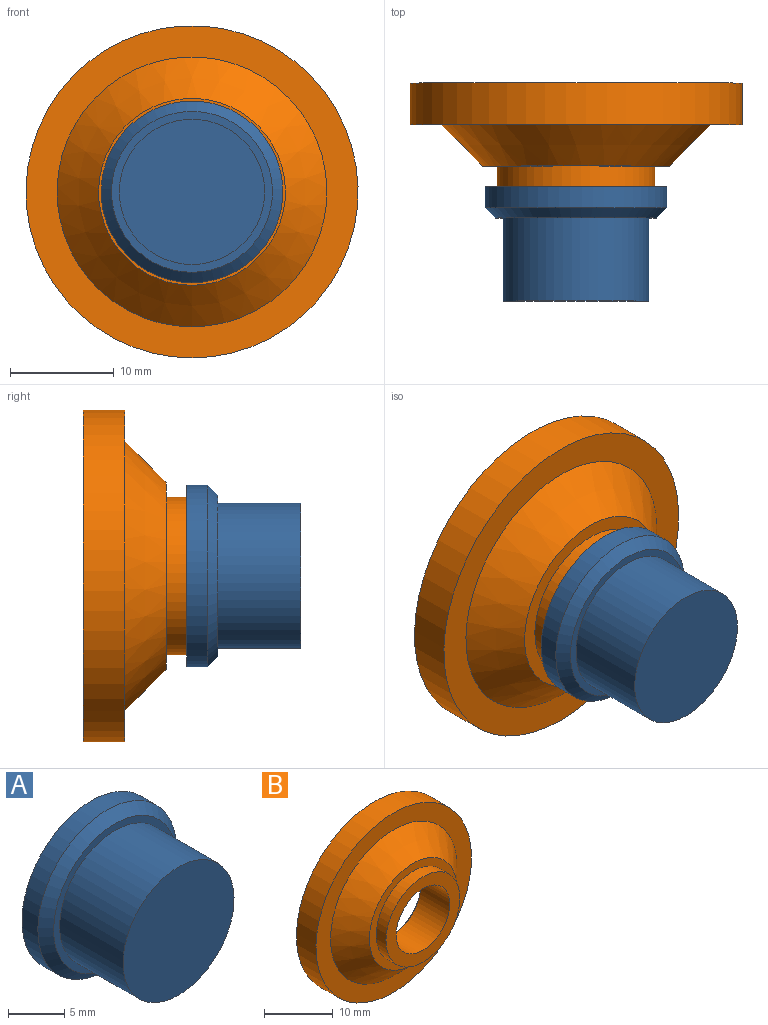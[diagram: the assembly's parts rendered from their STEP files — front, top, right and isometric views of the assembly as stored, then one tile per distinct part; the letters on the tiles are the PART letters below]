
ASSEMBLY  parts=2 mates=1
PART A: 6 faces, bbox 17.5x11x17.5 mm
  f0: cylinder r=8.75mm len=17.5mm, axis (0,1,0), area 110mm2, adj f2,f5
  f1: plane 15.5x15.5mm, normal (0,-1,0), area 34.8mm2, adj f3,f5
  f2: plane 17.5x17.5mm, normal (0,1,0), area 240.5mm2, adj f0
  f3: cylinder r=7mm len=14mm, axis (0,1,0), area 351.9mm2, adj f1,f4
  f4: plane 14x14mm, normal (0,-1,0), area 153.9mm2, adj f3
  f5: cone r=7.75mm half-angle=45deg, axis (0,1,0), area 73.3mm2, adj f0,f1
PART B: 10 faces, bbox 32x10x32 mm
  f0: cylinder r=5.5mm len=11mm, axis (0,1,0), area 207.3mm2, adj f2,f9
  f1: cylinder r=7.6mm len=15.2mm, axis (0,1,0), area 95.5mm2, adj f2,f4
  f2: plane 15.2x15.2mm, normal (0,-1,0), area 86.4mm2, adj f0,f1
  f3: plane 32x32mm, normal (0,1,0), area 424.1mm2, adj f6,f8
  f4: plane 18x18mm, normal (0,-1,0), area 73mm2, adj f1,f5
  f5: cone r=9mm half-angle=45deg, axis (0,1,0), area 391mm2, adj f4,f7
  f6: cylinder r=16mm len=32mm, axis (0,1,0), area 402.1mm2, adj f3,f7
  f7: plane 32x32mm, normal (0,-1,0), area 273.3mm2, adj f5,f6
  f8: cylinder r=11mm len=22mm, axis (0,1,0), area 276.5mm2, adj f3,f9
  f9: plane 22x22mm, normal (0,1,0), area 285.1mm2, adj f0,f8
PLACE A t=(-16.82,-3.26,-2.86)mm
PLACE B t=(-16.82,6.74,-2.86)mm
MATE fastened A.f0 <-> B.f8  axis (0,1,0) through (-16.82,-3.26,-2.86)mm
